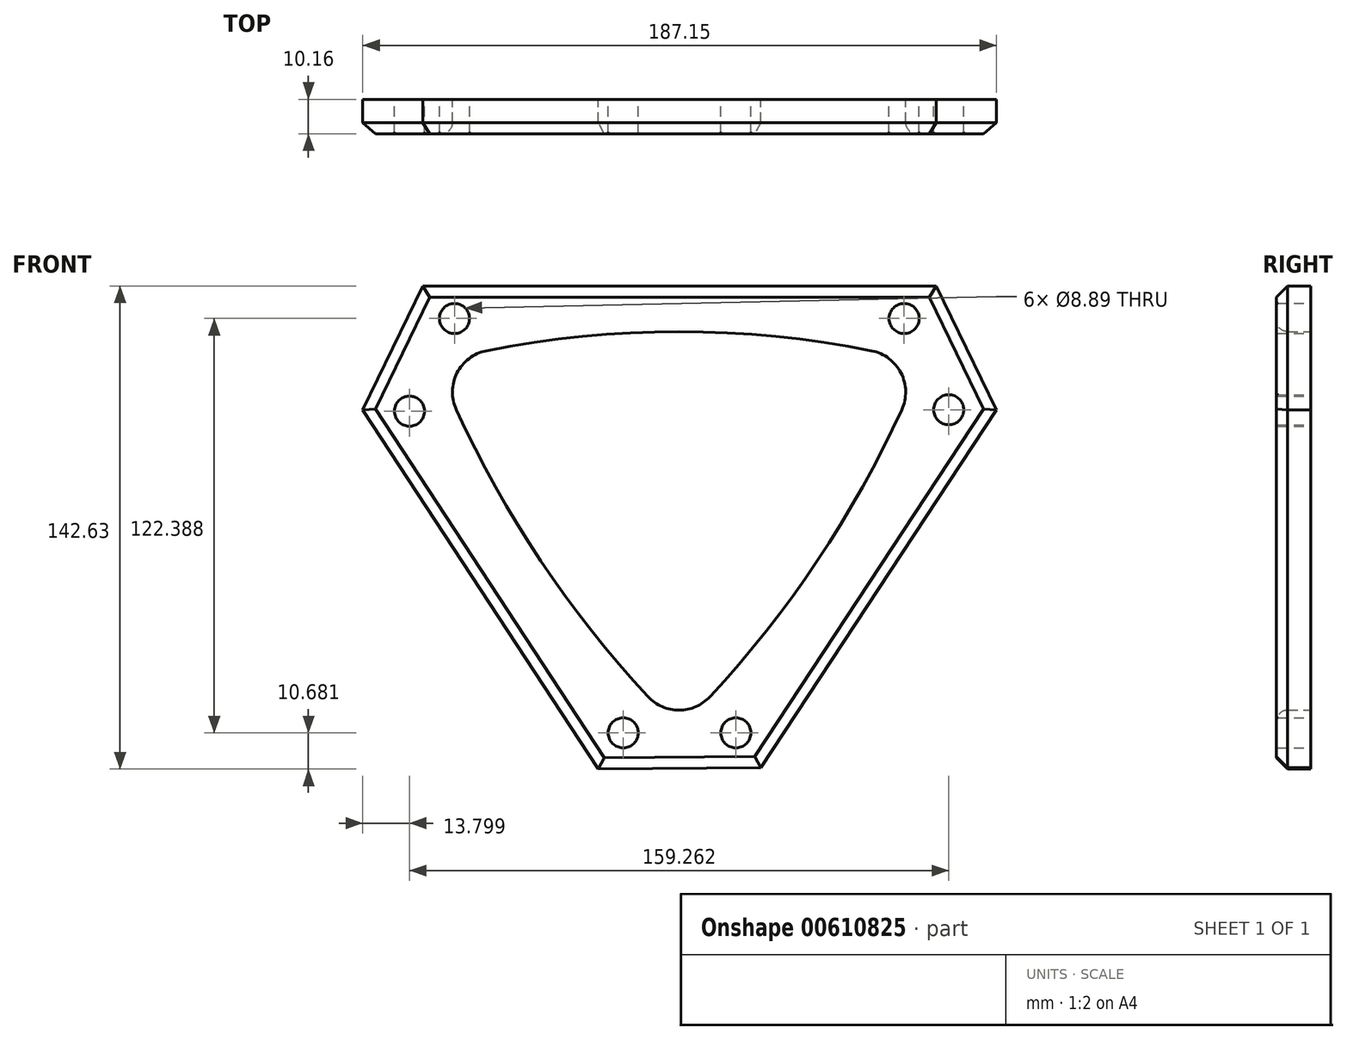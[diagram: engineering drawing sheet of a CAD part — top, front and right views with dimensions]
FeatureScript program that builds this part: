
annotation { "Feature Type Name" : "Feature", "Feature Type Description" : "" }
export const myFeature = defineFeature(function(context is Context, id is Id, definition is map)
    precondition{}
    {
        {
            var Q0;
            Q0=qCreatedBy(makeId("Front.planeOp"),FACE);
            var sketch = newSketch(context, id + "F0", { "sketchPlane" : qUnion([Q0])});
            skArc(sketch, "E0.0", {"start": v(56.94, 46.93) * mm, "mid": v(0, 52.61) * mm, "end": v(-56.95, 46.93) * mm});
            skArc(sketch, "E1.0", {"start": v(-56.95, 46.93) * mm, "mid": v(-65.58, 40.37) * mm, "end": v(-65.8, 29.54) * mm});
            skArc(sketch, "E2.0", {"start": v(-65.8, 29.54) * mm, "mid": v(-40.83, -15.1) * mm, "end": v(-9.12, -55.22) * mm});
            skArc(sketch, "E3.0", {"start": v(-9.12, -55.22) * mm, "mid": v(0, -59.2) * mm, "end": v(9.12, -55.22) * mm});
            skArc(sketch, "E4.0", {"start": v(9.12, -55.22) * mm, "mid": v(40.83, -15.1) * mm, "end": v(65.79, 29.54) * mm});
            skArc(sketch, "E5.0", {"start": v(65.79, 29.54) * mm, "mid": v(65.57, 40.37) * mm, "end": v(56.94, 46.93) * mm});
            skLineSegment(sketch, "E6", {"start": v(-75.68, 66.05) * mm, "end": v(76.02, 66.05) * mm});
            skLineSegment(sketch, "E7", {"start": v(24.15, -76.14) * mm, "end": v(-23.82, -76.58) * mm});
            skLineSegment(sketch, "E8", {"start": v(-75.68, 66.05) * mm, "end": v(-93.4, 29.54) * mm});
            skLineSegment(sketch, "E9", {"start": v(76.02, 66.05) * mm, "end": v(93.75, 29.54) * mm});
            skLineSegment(sketch, "E10", {"start": v(93.75, 29.54) * mm, "end": v(24.15, -76.14) * mm});
            skLineSegment(sketch, "E11", {"start": v(-93.4, 29.54) * mm, "end": v(-23.82, -76.58) * mm});
            skPoint(sketch, "E12.startSnap0", {"position": v(-16.47, -65.9) * mm});
            skCircle(sketch, "E13", {"center": v(-16.47, -65.9) * mm, "radius": 4.45 * mm});
            skCircle(sketch, "E14", {"center": v(16.8, -65.9) * mm, "radius": 4.45 * mm});
            skPoint(sketch, "E15.startSnap0", {"position": v(-66.32, 56.49) * mm});
            skCircle(sketch, "E16", {"center": v(-66.32, 56.49) * mm, "radius": 4.45 * mm});
            skCircle(sketch, "E17", {"center": v(66.48, 56.49) * mm, "radius": 4.45 * mm});
            skCircle(sketch, "E18", {"center": v(-79.6, 29.11) * mm, "radius": 4.45 * mm});
            skPoint(sketch, "E18.centerSnap0", {"position": v(-79.6, 29.54) * mm});
            skCircle(sketch, "E19", {"center": v(79.66, 29.54) * mm, "radius": 4.45 * mm});
            skSolve(sketch);
        }
        {
            var Q0;
            Q0 = qSketchRegion(id + "F0", true);
            extrude(context, id + "F1", {"entities" : qUnion([Q0]), "depth" : 10.16 * mm, "offsetDistance" : 25.4 * mm});
        }
        {
            var Q0;
            Q0=makeQuery(id+"F1.opExtrude","CAP_EDGE",EDGE,{"disambiguationData":[OSD([sQuery(id+"F0.wireOp",EDGE,"E8")])],"isStart":false});
            var Q1;
            Q1=makeQuery(id+"F1.opExtrude","CAP_EDGE",EDGE,{"disambiguationData":[OSD([sQuery(id+"F0.wireOp",EDGE,"E6")])],"isStart":false});
            var Q2;
            Q2=makeQuery(id+"F1.opExtrude","CAP_EDGE",EDGE,{"disambiguationData":[OSD([sQuery(id+"F0.wireOp",EDGE,"E7")])],"isStart":false});
            var Q3;
            Q3=makeQuery(id+"F1.opExtrude","CAP_EDGE",EDGE,{"disambiguationData":[OSD([sQuery(id+"F0.wireOp",EDGE,"E11")])],"isStart":false});
            var Q4;
            Q4=makeQuery(id+"F1.opExtrude","CAP_EDGE",EDGE,{"disambiguationData":[OSD([sQuery(id+"F0.wireOp",EDGE,"E10")])],"isStart":false});
            var Q5;
            Q5=makeQuery(id+"F1.opExtrude","CAP_EDGE",EDGE,{"disambiguationData":[OSD([sQuery(id+"F0.wireOp",EDGE,"E9")])],"isStart":false});
            chamfer(context, id + "F2", {"entities" : qUnion([Q0, Q1, Q2, Q3, Q4, Q5]), "width" : 3.3 * mm, "tangentPropagation" : true});
        }
        {
            var Q0;
            Q0=makeQuery(id+"F1.opExtrude","CAP_EDGE",EDGE,{"disambiguationData":[OSD([sQuery(id+"F0.wireOp",EDGE,"E0.0")])],"isStart":false});
            fillet(context, id + "F3", {"entities" : qUnion([Q0]), "radius" : 3.3 * mm, "tangentPropagation" : true, "allowEdgeOverflow" : false});
        }
        {
            var Q0;
            Q0=makeQuery(id+"F1.opExtrude","CAP_EDGE",EDGE,{"disambiguationData":[OSD([sQuery(id+"F0.wireOp",EDGE,"E18")])],"isStart":false});
            var Q1;
            Q1=makeQuery(id+"F1.opExtrude","CAP_EDGE",EDGE,{"disambiguationData":[OSD([sQuery(id+"F0.wireOp",EDGE,"E16")])],"isStart":false});
            var Q2;
            Q2=makeQuery(id+"F1.opExtrude","CAP_EDGE",EDGE,{"disambiguationData":[OSD([sQuery(id+"F0.wireOp",EDGE,"E17")])],"isStart":false});
            var Q3;
            Q3=makeQuery(id+"F1.opExtrude","CAP_EDGE",EDGE,{"disambiguationData":[OSD([sQuery(id+"F0.wireOp",EDGE,"E19")])],"isStart":false});
            var Q4;
            Q4=makeQuery(id+"F1.opExtrude","CAP_EDGE",EDGE,{"disambiguationData":[OSD([sQuery(id+"F0.wireOp",EDGE,"E13")])],"isStart":false});
            var Q5;
            Q5=makeQuery(id+"F1.opExtrude","CAP_EDGE",EDGE,{"disambiguationData":[OSD([sQuery(id+"F0.wireOp",EDGE,"E14")])],"isStart":false});
            fillet(context, id + "F4", {"entities" : qUnion([Q0, Q1, Q2, Q3, Q4, Q5]), "radius" : 0.5 * mm, "tangentPropagation" : true, "allowEdgeOverflow" : false});
        }
    });
